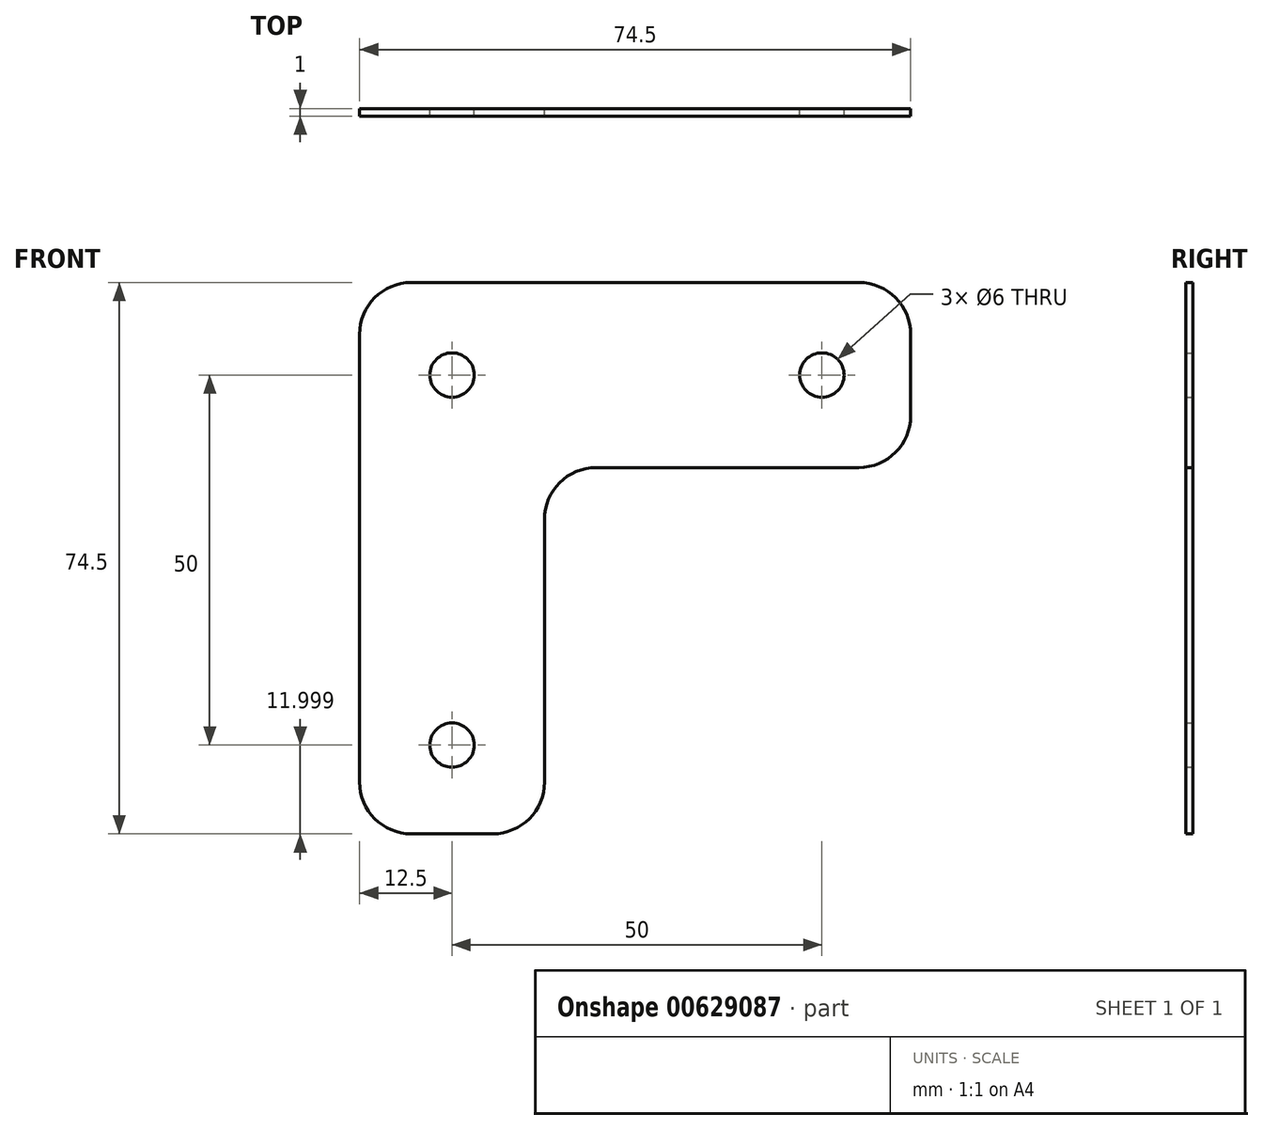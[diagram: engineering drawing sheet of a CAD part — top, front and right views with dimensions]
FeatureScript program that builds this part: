
annotation { "Feature Type Name" : "Feature", "Feature Type Description" : "" }
export const myFeature = defineFeature(function(context is Context, id is Id, definition is map)
    precondition{}
    {
        {
            var Q0;
            Q0=qCreatedBy(makeId("Front.planeOp"),FACE);
            var sketch = newSketch(context, id + "F0", { "sketchPlane" : qUnion([Q0])});
            skLineSegment(sketch, "E0", {"start": v(-54.1, -38.2) * mm, "end": v(-54.1, 22.3) * mm});
            skLineSegment(sketch, "E1", {"start": v(-47.1, 29.3) * mm, "end": v(13.4, 29.3) * mm});
            skLineSegment(sketch, "E2", {"start": v(20.4, 22.3) * mm, "end": v(20.4, 11.3) * mm});
            skLineSegment(sketch, "E3", {"start": v(13.4, 4.3) * mm, "end": v(-22.1, 4.3) * mm});
            skLineSegment(sketch, "E4", {"start": v(-29.1, -2.7) * mm, "end": v(-29.1, -38.2) * mm});
            skLineSegment(sketch, "E5", {"start": v(-36.1, -45.2) * mm, "end": v(-47.1, -45.2) * mm});
            skPoint(sketch, "E6.visualSharp", {"position": v(-54.1, 29.3) * mm});
            skArc(sketch, "E6.filletArc", {"start": v(-47.1, 29.3) * mm, "mid": v(-52.04, 27.26) * mm, "end": v(-54.1, 22.3) * mm});
            skPoint(sketch, "E7.visualSharp", {"position": v(20.4, 29.3) * mm});
            skArc(sketch, "E7.filletArc", {"start": v(20.4, 22.3) * mm, "mid": v(18.36, 27.26) * mm, "end": v(13.4, 29.3) * mm});
            skPoint(sketch, "E8.visualSharp", {"position": v(20.4, 4.3) * mm});
            skArc(sketch, "E8.filletArc", {"start": v(13.4, 4.3) * mm, "mid": v(18.36, 6.36) * mm, "end": v(20.4, 11.3) * mm});
            skPoint(sketch, "E9.visualSharp", {"position": v(-29.1, -45.2) * mm});
            skArc(sketch, "E9.filletArc", {"start": v(-36.1, -45.2) * mm, "mid": v(-31.14, -43.14) * mm, "end": v(-29.1, -38.2) * mm});
            skPoint(sketch, "E10.visualSharp", {"position": v(-54.1, -45.2) * mm});
            skArc(sketch, "E10.filletArc", {"start": v(-54.1, -38.2) * mm, "mid": v(-52.04, -43.14) * mm, "end": v(-47.1, -45.2) * mm});
            skPoint(sketch, "E11.visualSharp", {"position": v(-29.1, 4.3) * mm});
            skArc(sketch, "E11.filletArc", {"start": v(-22.1, 4.3) * mm, "mid": v(-27.04, 2.26) * mm, "end": v(-29.1, -2.7) * mm});
            skPoint(sketch, "E12", {"position": v(8.4, 16.8) * mm});
            skPoint(sketch, "E13", {"position": v(-41.6, 16.8) * mm});
            skPoint(sketch, "E14", {"position": v(-41.6, -33.2) * mm});
            skSolve(sketch);
        }
        {
            var Q0;
            Q0=qSketchRegion(id+"F0",true);
            extrude(context, id + "F1", {"entities" : qUnion([Q0]), "depth" : 1 * mm, "offsetDistance" : 25 * mm});
        }
        {
            var Q0;
            Q0=sQuery(id+"F0.wireOp",VERTEX,"E13");
            var Q1;
            Q1=sQuery(id+"F0.wireOp",VERTEX,"E12");
            var Q2;
            Q2=sQuery(id+"F0.wireOp",VERTEX,"E14");
            var Q3;
            Q3=makeQuery(id+"F1.opExtrude","SWEPT_BODY",BODY,{"disambiguationData":[OSD([sQuery(id+"F0.wireOp",EDGE,"E0"),sQuery(id+"F0.wireOp",EDGE,"E1"),sQuery(id+"F0.wireOp",EDGE,"E2"),sQuery(id+"F0.wireOp",EDGE,"E3"),sQuery(id+"F0.wireOp",EDGE,"E4"),sQuery(id+"F0.wireOp",EDGE,"E5"),sQuery(id+"F0.wireOp",EDGE,"E6.filletArc"),sQuery(id+"F0.wireOp",EDGE,"E7.filletArc"),sQuery(id+"F0.wireOp",EDGE,"E8.filletArc"),sQuery(id+"F0.wireOp",EDGE,"E9.filletArc"),sQuery(id+"F0.wireOp",EDGE,"E10.filletArc"),sQuery(id+"F0.wireOp",EDGE,"E11.filletArc")])]});
            hole(context, id + "F2", {"style" : HoleStyle.SIMPLE, "endStyle" : HoleEndStyle.THROUGH, "oppositeDirection" : true, "holeDiameter" : 6 * mm, "isTappedThrough" : true, "tappedDepth" : 12 * mm, "tapClearance" : 3, "locations" : qUnion([Q0, Q1, Q2]), "scope" : qUnion([Q3])});
        }
    });
